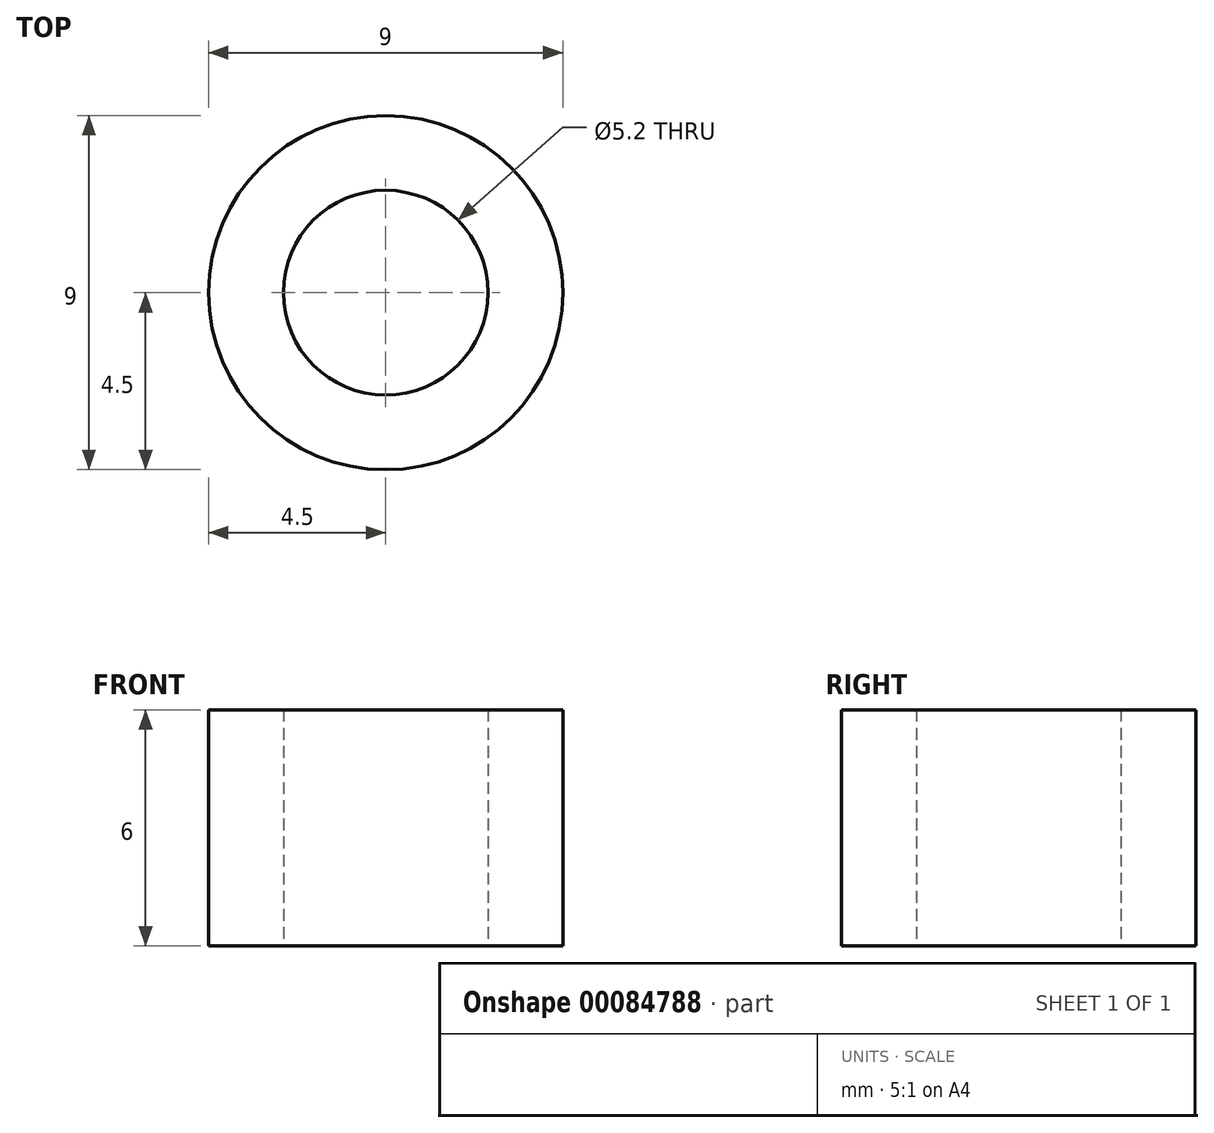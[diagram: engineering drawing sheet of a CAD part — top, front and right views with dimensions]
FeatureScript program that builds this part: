
annotation { "Feature Type Name" : "Feature", "Feature Type Description" : "" }
export const myFeature = defineFeature(function(context is Context, id is Id, definition is map)
    precondition{}
    {
        {
            var Q0;
            Q0=qCreatedBy(makeId("Top.planeOp"),FACE);
            var sketch = newSketch(context, id + "F0", { "sketchPlane" : qUnion([Q0])});
            skCircle(sketch, "E0", {"center": v(0, 0) * mm, "radius": 4.5 * mm});
            skCircle(sketch, "E1", {"center": v(0, 0) * mm, "radius": 2.6 * mm});
            skSolve(sketch);
        }
        {
            var Q0;
            Q0=makeQuery(id+"F0.imprint","IMPRINT",FACE,{"disambiguationData":[TD([[makeQuery(id+"F0.imprint","IMPRINT",EDGE,{"derivedFrom":sQuery(id+"F0.wireOp",EDGE,"E0")}),1.0]])]});
            extrude(context, id + "F1", {"entities" : qUnion([Q0]), "depth" : 6 * mm});
        }
    });
